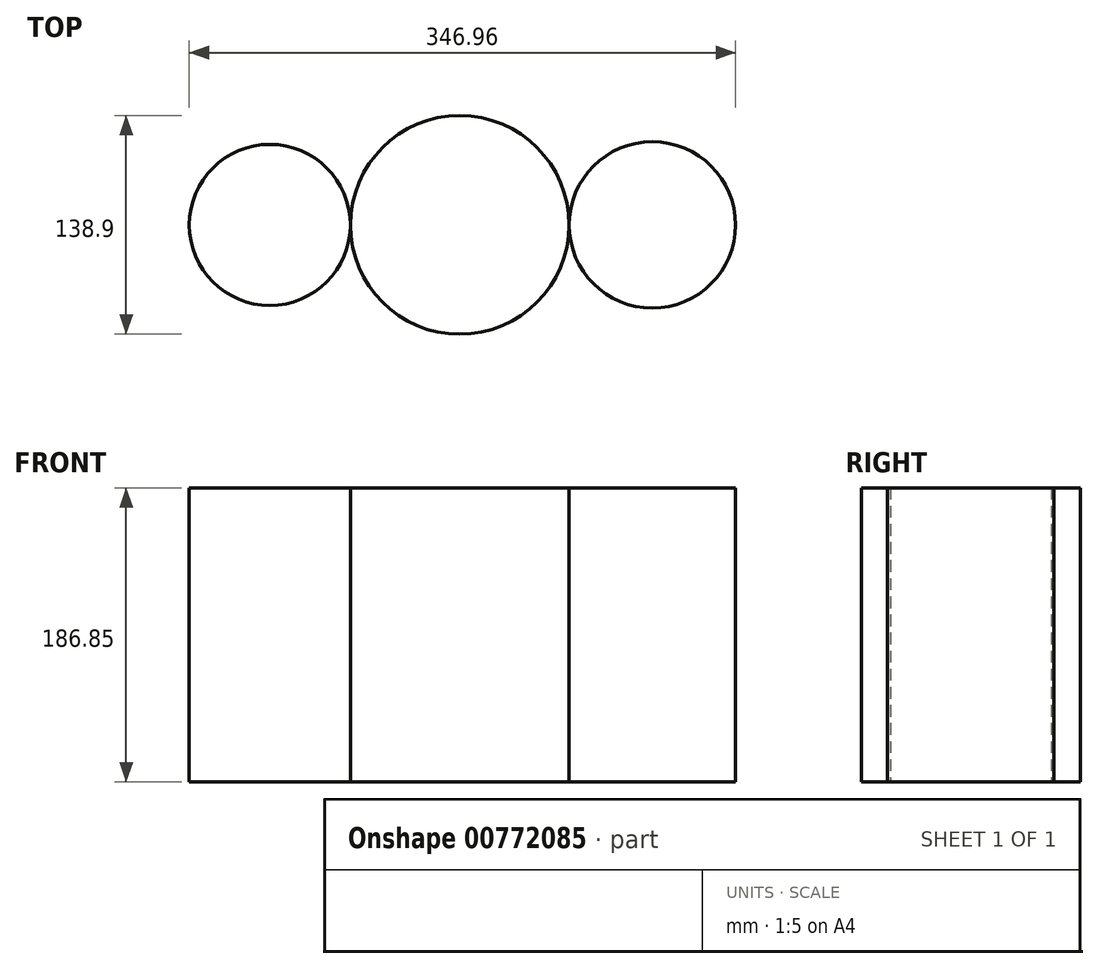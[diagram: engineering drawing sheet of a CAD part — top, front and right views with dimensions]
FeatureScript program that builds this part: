
annotation { "Feature Type Name" : "Feature", "Feature Type Description" : "" }
export const myFeature = defineFeature(function(context is Context, id is Id, definition is map)
    precondition{}
    {
        {
            var Q0;
            Q0=qCreatedBy(makeId("Top.planeOp"),FACE);
            var sketch = newSketch(context, id + "F0", { "sketchPlane" : qUnion([Q0])});
            skCircle(sketch, "E0", {"center": v(0, 0) * mm, "radius": 69.45 * mm});
            skCircle(sketch, "E1", {"center": v(-120.62, 0) * mm, "radius": 51.17 * mm});
            skCircle(sketch, "E2", {"center": v(122.3, 0) * mm, "radius": 52.86 * mm});
            skSolve(sketch);
        }
        {
            var Q0;
            Q0 = qSketchRegion(id + "F0", true);
            extrude(context, id + "F1", {"entities" : qUnion([Q0]), "depth" : 186.85 * mm, "offsetDistance" : 25.4 * mm});
        }
    });
